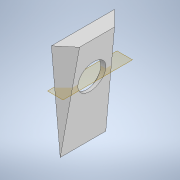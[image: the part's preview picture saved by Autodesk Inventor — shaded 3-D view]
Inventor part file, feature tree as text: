
AUTODESK INVENTOR PART (.ipt)
format: ipt  version: 2021 (Build 250183000, 183)  size: 415,744 bytes
history: native  units: in
note: dims shown in document units (in); Inventor stores cm internally (conversion verified against a paired STEP export)
features: extrude x7, sketch x7, plane x2
ambient origin geometry x8: Origin, YZ Plane, XZ Plane, XY Plane, X Axis, Y Axis, Z Axis, Center Point
bodies: Solid1 (feature_tree)
feature tree (16):
  extrude  "MainStructure"  Depth=0.5622in
  extrude  "PipeHole"  TaperAngle=0.0deg  [1 undecoded]
  extrude  "AngleForTopRelief"  TaperAngle=0.0deg  [1 undecoded]
  extrude  "TextForBack"  TaperAngle=0.0deg  [1 undecoded]
  extrude  "ReliefForHole"  Depth=0.375in TaperAngle=0.0deg
  extrude  "TextForSmallText"  TaperAngle=45.0deg  [1 undecoded]
  plane  "Work Plane1"
  extrude  "SideAngle"  Depth=2.5in
  plane  "Work Plane2"
  sketch  "Sketch1"  dims[d1=0.055in d2=0.5622in]
  sketch  "Sketch2"  dims[d4=0.0in d7=0.0in d8=0.0in]
  sketch  "Sketch6"  dims[d19=0.0in d20=0.0in d25=0.0in]
  sketch  "Sketch7"  dims[d28=0.0in d29=0.0in]
  sketch  "Sketch8"  dims[d35=0.375in d36=0.1in d37=0.0in]
  sketch  "Sketch9"  dims[d38=45.0deg d39=45.0deg]
  sketch  "Sketch10"  dims[d40=0.0in d41=0.0in d42=2.5in]
note: 4 required parameter values undecoded (feature->parameter linkage not recoverable at this tier; creation-order binding heuristic only, values carry confidence <= 0.55)
